# Revit family: 11118 Стальной фонарный столб «Яуза» В 3.0.1 со светильником Хоббика
name_source: partatom
category: Антураж
revit_build: Autodesk Revit 2018 (Build: 20180423_1000(x64)
units: mm (PartAtom-declared; Revit-internal decimal feet)

## family parameters
Всегда вертикально = Да
Источник визуального образа = Геометрия семейства
На основе рабочей плоскости = Нет
Общий = Нет
При загрузке вырезать с полостями = Нет
Точка расчета площади = Нет

## types (5) — shared parameters
URL = https://hobbyka.ru
Артикул товара = Арт. 11118
Группа модели = Светильники со стальными опорами
Длина = 817 мм
Изготовитель = ООО «Хоббика»
Изображение типоразмера = Стальной фонарный столб «Яуза» В 3.0.1 со светильником Арт 11118.jpg
Материал изделия = Сталь
Цвет каркаса = Сталь
Ширина = 200 мм

## per-type parameters (varying)
| type | Версия 3,1 м | Версия 3,6 м | Версия 4,1 м | Версия 4,6 м | Версия 6,0 м | Высота | Описание |
| Версия 3,1 м | Да | Нет | Нет | Нет | Нет | 3100 мм | Стальной фонарный столб «Яуза» В 3.0.1 со светильником. Версия 3,1 м |
| Версия 3,6 м | Нет | Да | Нет | Нет | Нет | 3600 мм | Стальной фонарный столб «Яуза» В 3.0.1 со светильником. Версия 3,6 м |
| Версия 4,1 м | Нет | Нет | Да | Нет | Нет | 4100 мм | Стальной фонарный столб «Яуза» В 3.0.1 со светильником. Версия 4,1 м |
| Версия 4,6 м | Нет | Нет | Нет | Да | Нет | 4600 мм | Стальной фонарный столб «Яуза» В 3.0.1 со светильником. Версия 4,6 м |
| Версия 6,0 м | Нет | Нет | Нет | Нет | Да | 6000 мм | Стальной фонарный столб «Яуза» В 3.0.1 со светильником. Версия 6,0 м |
